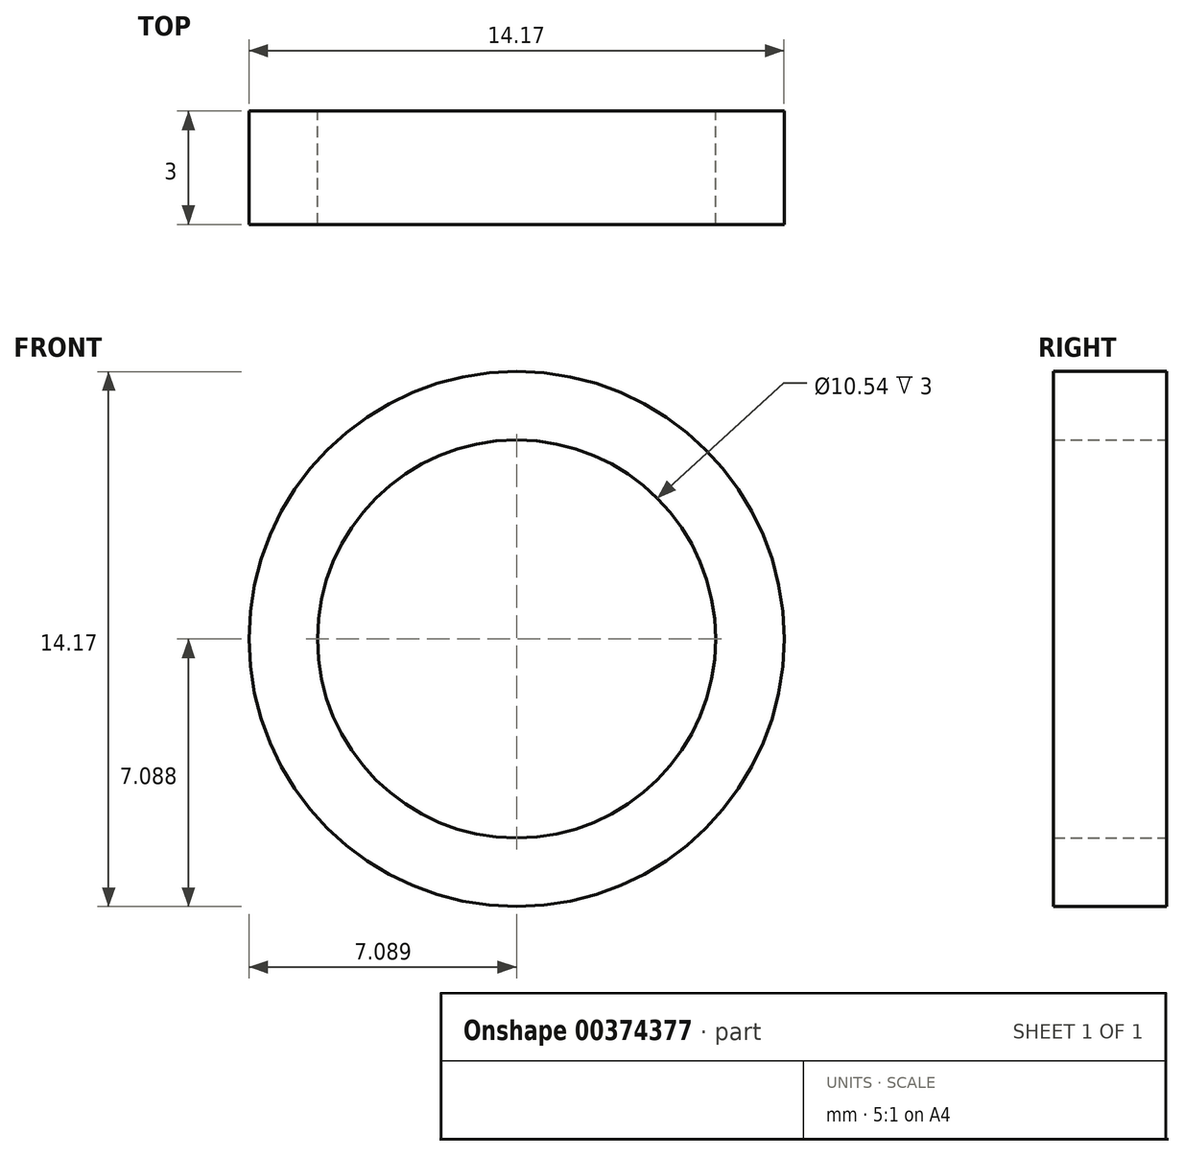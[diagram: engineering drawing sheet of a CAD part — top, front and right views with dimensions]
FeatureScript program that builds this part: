
annotation { "Feature Type Name" : "Feature", "Feature Type Description" : "" }
export const myFeature = defineFeature(function(context is Context, id is Id, definition is map)
    precondition{}
    {
        {
            var Q0;
            Q0=qCreatedBy(makeId("Front.planeOp"),FACE);
            var sketch = newSketch(context, id + "F0", { "sketchPlane" : qUnion([Q0])});
            skLineSegment(sketch, "E0", {"start": v(-6.35, 27.05) * mm, "end": v(-19, 0) * mm});
            skLineSegment(sketch, "E1", {"start": v(-19, 0) * mm, "end": v(-5.49, -29) * mm});
            skLineSegment(sketch, "E2", {"start": v(0, -40.8) * mm, "end": v(3.19, -33.95) * mm});
            skLineSegment(sketch, "E3", {"start": v(19, 0) * mm, "end": v(6.56, 26.82) * mm});
            skLineSegment(sketch, "E4", {"start": v(0, -40.8) * mm, "end": v(-4.22, -31.73) * mm});
            skLineSegment(sketch, "E5.trimOffspring", {"start": v(-4.05, -32.1) * mm, "end": v(0, -40.8) * mm});
            skLineSegment(sketch, "E6", {"start": v(19, 0) * mm, "end": v(7.6, -24.48) * mm});
            skLineSegment(sketch, "E7.trimOffspring", {"start": v(7.6, -24.48) * mm, "end": v(19, 0) * mm});
            skLineSegment(sketch, "E8", {"start": v(0, -35.8) * mm, "end": v(0, -40.8) * mm, "construction": true});
            skLineSegment(sketch, "E9", {"start": v(-4.22, -31.73) * mm, "end": v(-3.22, -31.73) * mm, "construction": true});
            skLineSegment(sketch, "E10", {"start": v(0, -40.8) * mm, "end": v(0, -27.8) * mm, "construction": true});
            skLineSegment(sketch, "E11", {"start": v(-3.03, -31.5) * mm, "end": v(-0.33, -28.2) * mm});
            skLineSegment(sketch, "E12", {"start": v(0, -27.8) * mm, "end": v(-1.3, -27.8) * mm, "construction": true});
            skLineSegment(sketch, "E13", {"start": v(-3.97, -31.4) * mm, "end": v(-1.51, -28.08) * mm});
            skLineSegment(sketch, "E14", {"start": v(-5.49, -29) * mm, "end": v(-5.49, -18) * mm});
            skLineSegment(sketch, "E15", {"start": v(-19, 0) * mm, "end": v(-12, 0) * mm, "construction": true});
            skLineSegment(sketch, "E16", {"start": v(-11.92, 0.33) * mm, "end": v(-9.47, 10.21) * mm});
            skLineSegment(sketch, "E17", {"start": v(-12, 0) * mm, "end": v(-7, 0) * mm, "construction": true});
            skFitSpline(sketch, "E18", {"points": [v(-12, 0) * mm, v(-9.5, -0.75) * mm, v(-7, 0) * mm], "startDerivative": vector(4.82, -3.74) * mm, "endDerivative": vector(5.18, 3.7) * mm});
            skPoint(sketch, "E19.endSnap0", {"position": v(-9.5, 0) * mm});
            skLineSegment(sketch, "E20", {"start": v(12, 0) * mm, "end": v(19, 0) * mm, "construction": true});
            skLineSegment(sketch, "E21", {"start": v(12, 0) * mm, "end": v(7, 0) * mm, "construction": true});
            skFitSpline(sketch, "E22", {"points": [v(12, 0) * mm, v(9.62, -0.75) * mm, v(7, 0) * mm], "startDerivative": vector(-4.98, -2.8) * mm, "endDerivative": vector(-5.02, 2.8) * mm});
            skLineSegment(sketch, "E23", {"start": v(8.5, 0) * mm, "end": v(8.5, 2) * mm, "construction": true});
            skFitSpline(sketch, "E24", {"points": [v(7, 0) * mm, v(7.07, 1.14) * mm, v(8.5, 2) * mm], "startDerivative": vector(-1.68, 2.5) * mm, "endDerivative": vector(3.9, 0.71) * mm});
            skFitSpline(sketch, "E25.MirrorCS", {"points": [v(-7, 0) * mm, v(-7.07, 1.14) * mm, v(-8.5, 2) * mm], "startDerivative": vector(1.68, 2.5) * mm, "endDerivative": vector(-3.9, 0.71) * mm});
            skLineSegment(sketch, "E26", {"start": v(-8.5, 0) * mm, "end": v(-4.5, 0) * mm, "construction": true});
            skFitSpline(sketch, "E27", {"points": [v(-8.5, 2) * mm, v(-6.28, 1.54) * mm, v(-4.5, 0) * mm], "startDerivative": vector(5.18, 0.66) * mm, "endDerivative": vector(3.65, -3.27) * mm});
            skLineSegment(sketch, "E28", {"start": v(0, 0) * mm, "end": v(-3, 0) * mm, "construction": true});
            skFitSpline(sketch, "E29", {"points": [v(-4.5, 0) * mm, v(-4.95, 1.33) * mm, v(-3, 0) * mm], "startDerivative": vector(3.35, 3.5) * mm, "endDerivative": vector(3.99, -5.16) * mm});
            skFitSpline(sketch, "E30.MirrorCS", {"points": [v(8.5, 2) * mm, v(6.28, 1.54) * mm, v(4.5, 0) * mm], "startDerivative": vector(-5.18, 0.66) * mm, "endDerivative": vector(-3.65, -3.27) * mm});
            skFitSpline(sketch, "E31.MirrorCS", {"points": [v(4.5, 0) * mm, v(4.95, 1.33) * mm, v(3, 0) * mm], "startDerivative": vector(-3.35, 3.5) * mm, "endDerivative": vector(-3.99, -5.16) * mm});
            skPoint(sketch, "E32.visualSharp", {"position": v(-4.22, -31.73) * mm});
            skArc(sketch, "E32.filletArc", {"start": v(-3.97, -31.4) * mm, "mid": v(-4.1, -31.74) * mm, "end": v(-4.05, -32.1) * mm});
            skFitSpline(sketch, "E33", {"points": [v(3.38, -33.54) * mm, v(0, -35.8) * mm, v(-3.22, -31.73) * mm], "startDerivative": vector(-8.47, -7.22) * mm, "endDerivative": vector(-9, 21.79) * mm});
            skArc(sketch, "E34.filletArc", {"start": v(-3.03, -31.5) * mm, "mid": v(-3.14, -31.74) * mm, "end": v(-3.1, -32) * mm});
            skLineSegment(sketch, "E35.MirrorCS", {"start": v(11.9, 0.38) * mm, "end": v(9.47, 10.21) * mm});
            skArc(sketch, "E36.filletArc", {"start": v(3.19, -33.95) * mm, "mid": v(3.16, -33.83) * mm, "end": v(3.03, -33.83) * mm});
            skArc(sketch, "E37.filletArc", {"start": v(-11.92, 0.33) * mm, "mid": v(-11.9, 0.02) * mm, "end": v(-11.7, -0.21) * mm});
            skArc(sketch, "E38.filletArc", {"start": v(11.65, -0.19) * mm, "mid": v(11.88, 0.05) * mm, "end": v(11.9, 0.38) * mm});
            skLineSegment(sketch, "E39", {"start": v(-19, -3.92) * mm, "end": v(-9, -3.92) * mm, "construction": true});
            skFitSpline(sketch, "E40", {"points": [v(-5.49, -18) * mm, v(-8.04, -16.8) * mm, v(-8.7, -15.8) * mm, v(-9.2, -15.1) * mm, v(-9.34, -14.03) * mm, v(-8.95, -9.14) * mm, v(-9.32, -7.89) * mm, v(-9.32, -7.89) * mm, v(-8.55, -8) * mm, v(-7.7, -8.28) * mm, v(-6.44, -9.3) * mm, v(-5.49, -11.37) * mm, v(-5.49, -11.37) * mm], "startDerivative": vector(-45.96, 0.73) * mm, "endDerivative": vector(-0.1, 1.46) * mm});
            skLineSegment(sketch, "E41", {"start": v(-5.49, -11.21) * mm, "end": v(-5.49, -9.58) * mm});
            skArc(sketch, "E42.filletArc", {"start": v(-5.55, -11.22) * mm, "mid": v(-5.51, -11.24) * mm, "end": v(-5.49, -11.21) * mm});
            skFitSpline(sketch, "E43", {"points": [v(-5.49, -9.58) * mm, v(-5.49, -8) * mm, v(-5.49, -7.89) * mm], "startDerivative": vector(0, 1.7) * mm, "endDerivative": vector(0, 1.7) * mm});
            skFitSpline(sketch, "E44.MirrorCS", {"points": [v(5.49, -18) * mm, v(8.04, -16.8) * mm, v(8.7, -15.8) * mm, v(9.2, -15.1) * mm, v(9.34, -14.03) * mm, v(8.95, -9.14) * mm, v(9.32, -7.89) * mm, v(9.32, -7.89) * mm, v(8.55, -8) * mm, v(7.7, -8.28) * mm, v(6.44, -9.3) * mm, v(5.49, -11.37) * mm, v(5.49, -11.37) * mm], "startDerivative": vector(45.96, 0.73) * mm, "endDerivative": vector(0.1, 1.46) * mm});
            skLineSegment(sketch, "E45.MirrorCS", {"start": v(5.49, -11.21) * mm, "end": v(5.49, -9.58) * mm});
            skFitSpline(sketch, "E46.MirrorCS", {"points": [v(5.49, -9.58) * mm, v(5.49, -8) * mm, v(5.49, -7.89) * mm], "startDerivative": vector(0, 1.7) * mm, "endDerivative": vector(0, 1.7) * mm});
            skLineSegment(sketch, "E47", {"start": v(5.49, -18) * mm, "end": v(5.49, -24.95) * mm});
            skFitSpline(sketch, "E48", {"points": [v(7.6, -24.48) * mm, v(6.87, -24.62) * mm, v(6.49, -24.93) * mm, v(5.49, -24.95) * mm], "startDerivative": vector(-2.44, -0.19) * mm, "endDerivative": vector(-2.97, 0.32) * mm});
            skLineSegment(sketch, "E49", {"start": v(-5.49, -29) * mm, "end": v(-5.49, -23.46) * mm});
            skLineSegment(sketch, "E50", {"start": v(-5.49, -23.46) * mm, "end": v(-2.66, -23.46) * mm, "construction": true});
            skLineSegment(sketch, "E51", {"start": v(-1.4, -27.45) * mm, "end": v(-2.48, -24.05) * mm});
            skLineSegment(sketch, "E52", {"start": v(-0.14, -27.3) * mm, "end": v(-1.09, -23.9) * mm});
            skLineSegment(sketch, "E53", {"start": v(-0.96, -23.08) * mm, "end": v(2.43, -18) * mm});
            skLineSegment(sketch, "E54", {"start": v(-2.38, -22.91) * mm, "end": v(0.13, -18) * mm});
            skArc(sketch, "E55.filletArc", {"start": v(-2.38, -22.91) * mm, "mid": v(-2.54, -23.47) * mm, "end": v(-2.48, -24.05) * mm});
            skPoint(sketch, "E56.visualSharp", {"position": v(-1.21, -23.46) * mm});
            skArc(sketch, "E56.filletArc", {"start": v(-0.96, -23.08) * mm, "mid": v(-1.11, -23.48) * mm, "end": v(-1.09, -23.9) * mm});
            skPoint(sketch, "E57.visualSharp", {"position": v(0, -27.8) * mm});
            skArc(sketch, "E57.filletArc", {"start": v(-0.33, -28.2) * mm, "mid": v(-0.12, -27.77) * mm, "end": v(-0.14, -27.3) * mm});
            skPoint(sketch, "E58.visualSharp", {"position": v(-1.3, -27.8) * mm});
            skArc(sketch, "E58.filletArc", {"start": v(-1.51, -28.08) * mm, "mid": v(-1.38, -27.78) * mm, "end": v(-1.4, -27.45) * mm});
            skFitSpline(sketch, "E59", {"points": [v(2.43, -18) * mm, v(2.43, -14.47) * mm, v(2.55, -12) * mm, v(5.49, -7.89) * mm], "startDerivative": vector(6.6, 8.09) * mm, "endDerivative": vector(13.28, 9.36) * mm});
            skFitSpline(sketch, "E60", {"points": [v(0.13, -18) * mm, v(-0.3, -13.02) * mm, v(-5.49, -7.89) * mm], "startDerivative": vector(2.11, 3.05) * mm, "endDerivative": vector(-11.71, 8.94) * mm});
            skFitSpline(sketch, "E61", {"points": [v(-6.23, 24.05) * mm, v(-4.65, 21.7) * mm, v(-5.31, 22.14) * mm, v(-6.43, 22.51) * mm], "startDerivative": vector(5.47, -7.52) * mm, "endDerivative": vector(-3.77, 0.76) * mm});
            skFitSpline(sketch, "E62.MirrorCS", {"points": [v(6.23, 24.05) * mm, v(4.65, 21.7) * mm, v(5.31, 22.14) * mm, v(6.43, 22.51) * mm], "startDerivative": vector(-5.47, -7.52) * mm, "endDerivative": vector(3.77, 0.76) * mm});
            skFitSpline(sketch, "E63", {"points": [v(-8.85, 12.72) * mm, v(-7.05, 11.65) * mm, v(-6.1, 9.92) * mm, v(-5.93, 9.21) * mm, v(-6.54, 9.82) * mm, v(-8.37, 10.7) * mm, v(-9.47, 10.21) * mm, v(-9.49, 10.16) * mm], "startDerivative": vector(10.13, -4.42) * mm, "endDerivative": vector(0.2, -1.36) * mm});
            skLineSegment(sketch, "E64.trimOffspring", {"start": v(-8.85, 12.72) * mm, "end": v(-6.43, 22.51) * mm});
            skFitSpline(sketch, "E65.MirrorCS", {"points": [v(8.85, 12.72) * mm, v(7.05, 11.65) * mm, v(6.1, 9.92) * mm, v(5.93, 9.21) * mm, v(6.54, 9.82) * mm, v(8.37, 10.7) * mm, v(9.47, 10.21) * mm, v(9.49, 10.16) * mm], "startDerivative": vector(-10.13, -4.42) * mm, "endDerivative": vector(-0.2, -1.36) * mm});
            skLineSegment(sketch, "E66.trimOffspring", {"start": v(8.85, 12.72) * mm, "end": v(6.43, 22.51) * mm});
            skFitSpline(sketch, "E67", {"points": [v(3, 0) * mm, v(2.42, 1.6) * mm, v(0.72, 4.24) * mm, v(-0.92, 5.83) * mm, v(-1.33, 7.26) * mm, v(-0.52, 8.85) * mm, v(1.42, 9.4) * mm, v(5.44, 11.82) * mm, v(6.3, 15.16) * mm, v(4.1, 17.4) * mm, v(2.37, 17.83) * mm, v(1.15, 17.67) * mm], "startDerivative": vector(-3.68, 16.9) * mm, "endDerivative": vector(-28.7, -4.78) * mm});
            skFitSpline(sketch, "E68", {"points": [v(-3, 0) * mm, v(-4.1, 5.1) * mm, v(-4.16, 7.15) * mm, v(-3, 9.42) * mm, v(1.13, 10.87) * mm, v(4.54, 12.41) * mm, v(5.6, 14.87) * mm, v(3.7, 16.65) * mm, v(0.6, 16.79) * mm, v(-0.96, 15.66) * mm, v(-1.59, 14.48) * mm, v(-1.54, 13.95) * mm, v(-2.14, 14.27) * mm], "startDerivative": vector(-10.38, 44.16) * mm, "endDerivative": vector(-16.47, 11.68) * mm});
            skLineSegment(sketch, "E69", {"start": v(-2.14, 14.27) * mm, "end": v(-2.43, 15.32) * mm});
            skLineSegment(sketch, "E70", {"start": v(-2.43, 15.32) * mm, "end": v(-2.14, 16.5) * mm});
            skLineSegment(sketch, "E71", {"start": v(-2.14, 16.5) * mm, "end": v(-2.38, 17.15) * mm});
            skLineSegment(sketch, "E72", {"start": v(-2.38, 17.15) * mm, "end": v(-1.4, 18.98) * mm});
            skLineSegment(sketch, "E73", {"start": v(-1.4, 18.98) * mm, "end": v(-2.14, 21.62) * mm});
            skFitSpline(sketch, "E74", {"points": [v(-2.14, 21.62) * mm, v(-2.14, 21.91) * mm, v(-1.99, 22.31) * mm, v(-1.86, 22.43) * mm, v(-1.86, 22.2) * mm, v(-1.74, 21.62) * mm, v(-0.63, 18.84) * mm], "startDerivative": vector(-0.2, 2.36) * mm, "endDerivative": vector(3.66, -8.74) * mm});
            skFitSpline(sketch, "E75", {"points": [v(-0.63, 18.84) * mm, v(2.44, 19.24) * mm, v(3.34, 19.69) * mm, v(3.62, 20.14) * mm, v(3.74, 20.26) * mm, v(3.69, 19.96) * mm, v(3.56, 19.44) * mm, v(2.76, 18.84) * mm, v(1.04, 18.3) * mm, v(0.76, 17.67) * mm, v(0.73, 17.56) * mm], "startDerivative": vector(17.18, 1.57) * mm, "endDerivative": vector(-0.66, -2.2) * mm});
            skLineSegment(sketch, "E76", {"start": v(0.73, 17.56) * mm, "end": v(1.15, 17.67) * mm});
            skLineSegment(sketch, "E77", {"start": v(5.49, -11.21) * mm, "end": v(5.49, -11.34) * mm});
            skLineSegment(sketch, "E78", {"start": v(5.49, -11.34) * mm, "end": v(5.55, -11.22) * mm});
            skLineSegment(sketch, "E79", {"start": v(6.35, 27.05) * mm, "end": v(6.4, 27.17) * mm});
            skLineSegment(sketch, "E80", {"start": v(6.56, 26.82) * mm, "end": v(6.4, 27.17) * mm});
            skCircle(sketch, "E81", {"center": v(-0.01, 30.2) * mm, "radius": 7.09 * mm});
            skPoint(sketch, "E81.third.point", {"position": v(3.93, 36.1) * mm});
            skCircle(sketch, "E82", {"center": v(-0.01, 30.2) * mm, "radius": 5.27 * mm});
            skPoint(sketch, "E83.orphan", {"position": v(-6.26, 26.35) * mm});
            skPoint(sketch, "E84.MirrorCS.0.internal.orphan", {"position": v(6.26, 23.2) * mm});
            skPoint(sketch, "E84.MirrorCS.1.internal.orphan", {"position": v(6.26, 26.35) * mm});
            skPoint(sketch, "E85.0.internal.orphan", {"position": v(-6.26, 23.2) * mm});
            skPoint(sketch, "E85.endDerivative.orphan", {"position": v(-6.26, 26.82) * mm});
            skLineSegment(sketch, "E86", {"start": v(-6.23, 24.05) * mm, "end": v(-6.08, 25.24) * mm});
            skLineSegment(sketch, "E87", {"start": v(-6.08, 25.24) * mm, "end": v(-4.77, 24.96) * mm});
            skLineSegment(sketch, "E88", {"start": v(6.05, 25.24) * mm, "end": v(6.23, 24.05) * mm});
            skLineSegment(sketch, "E89", {"start": v(4.75, 24.96) * mm, "end": v(6.05, 25.24) * mm});
            skSolve(sketch);
        }
        {
            var Q0;
            {var subQ0=sQuery(id+"F0.wireOp",EDGE,"E0");Q0=makeQuery(id+"F0.imprint","IMPRINT",FACE,{"disambiguationData":[TD([[makeQuery(id+"F0.imprint","IMPRINT",EDGE,{"derivedFrom":subQ0}),1.0]])]});}
            var Q1;
            Q1=makeQuery(id+"F0.imprint","IMPRINT",FACE,{"disambiguationData":[TD([[makeQuery(id+"F0.imprint","IMPRINT",EDGE,{"derivedFrom":sQuery(id+"F0.wireOp",EDGE,"E82")}),-1.0]])]});
            extrude(context, id + "F1", {"entities" : qUnion([Q0, Q1]), "depth" : 3 * mm});
        }
    });
